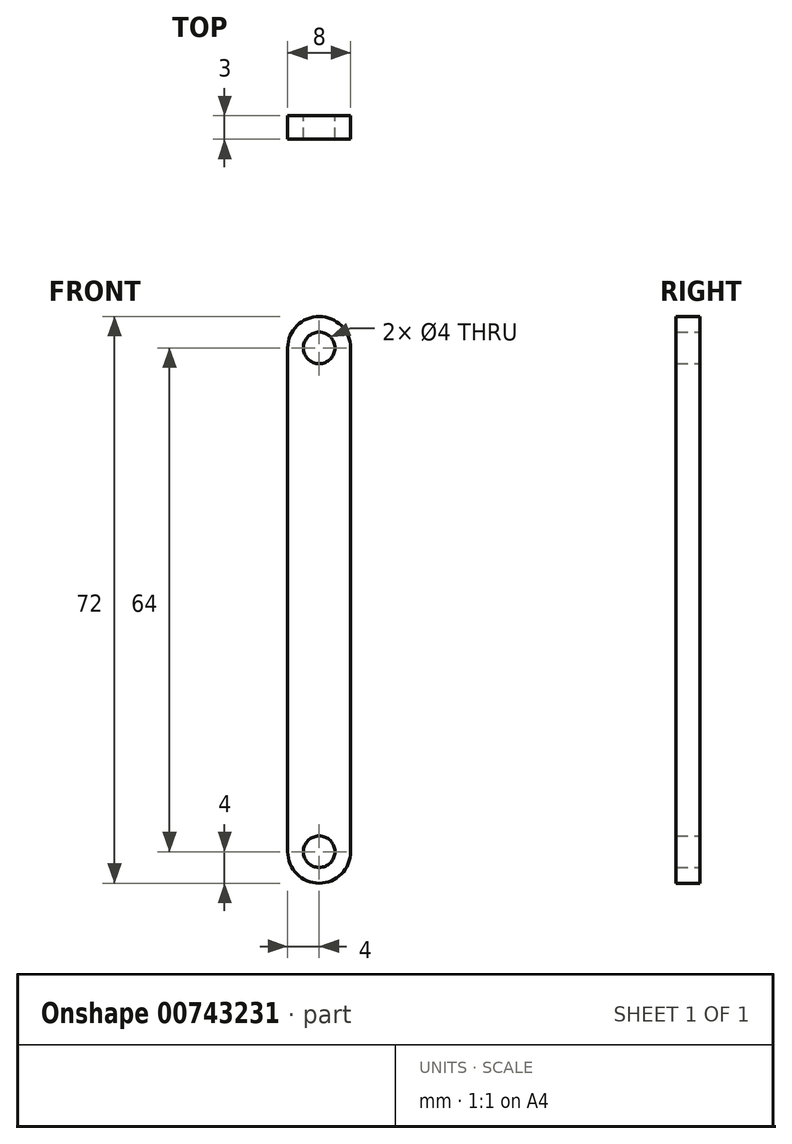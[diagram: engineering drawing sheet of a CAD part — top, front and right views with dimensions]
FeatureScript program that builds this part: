
annotation { "Feature Type Name" : "Feature", "Feature Type Description" : "" }
export const myFeature = defineFeature(function(context is Context, id is Id, definition is map)
    precondition{}
    {
        {
            var Q0;
            Q0=qCreatedBy(makeId("Front.planeOp"),FACE);
            var sketch = newSketch(context, id + "F0", { "sketchPlane" : qUnion([Q0])});
            skLineSegment(sketch, "E0.bottom", {"start": v(4, 32) * mm, "end": v(-4, 32) * mm, "construction": true});
            skLineSegment(sketch, "E0.top", {"start": v(4, -32) * mm, "end": v(-4, -32) * mm, "construction": true});
            skLineSegment(sketch, "E0.left", {"start": v(4, 32) * mm, "end": v(4, -32) * mm});
            skLineSegment(sketch, "E0.right", {"start": v(-4, 32) * mm, "end": v(-4, -32) * mm});
            skPoint(sketch, "E0.middle", {"position": v(0, 0) * mm});
            skArc(sketch, "E1", {"start": v(-4, -32) * mm, "mid": v(0, -36) * mm, "end": v(4, -32) * mm});
            skArc(sketch, "E2", {"start": v(4, 32) * mm, "mid": v(0, 36) * mm, "end": v(-4, 32) * mm});
            skCircle(sketch, "E3", {"center": v(0, 32) * mm, "radius": 2 * mm});
            skCircle(sketch, "E4", {"center": v(0, -32) * mm, "radius": 2 * mm});
            skSolve(sketch);
        }
        {
            var Q0;
            Q0=qSketchRegion(id+"F0",true);
            extrude(context, id + "F1", {"entities" : qUnion([Q0]), "depth" : 3 * mm, "offsetDistance" : 25 * mm});
        }
    });
